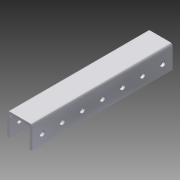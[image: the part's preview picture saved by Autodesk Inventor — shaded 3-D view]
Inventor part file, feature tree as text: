
AUTODESK INVENTOR PART (.ipt)
format: ipt  version: 2015 (Build 190159000, 159)  size: 413,184 bytes
history: native  units: in
note: dims shown in document units (in); Inventor stores cm internally (conversion verified against a paired STEP export)
features: extrude x2, sketch x2, pattern_linear x1
ambient origin geometry x8: Origin, YZ Plane, XZ Plane, XY Plane, X Axis, Y Axis, Z Axis, Center Point
bodies: Solid1 (feature_tree)
feature tree (5):
  extrude  "Extrusion1"  Depth=7.0in
  extrude  "Extrusion4"  Depth=0.5in
  pattern_linear  "Rectangular Pattern3"  Spacing1=0.0in  [1 undecoded]
  sketch  "Sketch1"  dims[d0=1.13in d1=1.25in d2=0.125in d3=0.125in d4=0.125in d5=7.0in]
  sketch  "Sketch4"  dims[d6=0.0in d34=0.5in d35=0.0in d36=0.25in d37=1.0in d38=0.0in d39=11.811in d41=1.0in d42=11.811in d44=1.0in]
note: 1 required parameter value undecoded (feature->parameter linkage not recoverable at this tier; creation-order binding heuristic only, values carry confidence <= 0.55)
